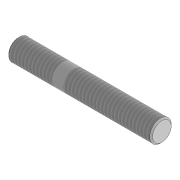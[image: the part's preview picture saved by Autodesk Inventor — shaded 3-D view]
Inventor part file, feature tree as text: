
AUTODESK INVENTOR PART (.ipt)
format: ipt  version: 2022.5 (Build 265521000, 521)  size: 83,968 bytes
history: native  units: mm
features: thread x2, extrude x1, chamfer x1, sketch x1
ambient origin geometry x8: Origin, YZ Plane, XZ Plane, XY Plane, X Axis, Y Axis, Z Axis, Center Point
bodies: Body1 (feature_tree)
feature tree (5):
  extrude  "Extrusion2"  Depth=20.0mm TaperAngle=0.0deg
  chamfer  "Chamfer1"  Distance=0.2mm Angle=45.0deg
  thread  "Thread1"  [1 undecoded]
  thread  "Thread2"  [1 undecoded]
  sketch  "Sketch2"  dims[d9=3.0mm d10=20.0mm d11=0.0mm d12=0.2mm d13=2.0mm d14=45.0deg d15=6.0mm d16=0.0mm d17=12.0mm d18=0.0mm]
note: 2 required parameter values undecoded (feature->parameter linkage not recoverable at this tier; creation-order binding heuristic only, values carry confidence <= 0.55)
